# Revit family: 303_R412PX_
name_source: partatom
category: Pipe Accessories
revit_build: Autodesk Revit 2018 (Build: 20170223_1515(x64)
units: mm (PartAtom-declared; Revit-internal decimal feet)

## family parameters
Always vertical = Yes
Cut with Voids When Loaded = No
Part Type = Valve - Breaks Into
Round Connector Dimension = Use Diameter
Shared = No
Work Plane-Based = No

## types (2) — shared parameters
CAT0 = Yes
CenSd_W2_6 = 13 mm  [stored 0.0426509 ft]
D = 16 mm
D3 = 13 mm  [stored 0.0426509 ft]
Description = Straight valve with precision adjustment numberscale and protection cap, with connectoin of adapter for pipe
J12 = 5 mm  [stored 0.0164042 ft]
J12__ve = -5 mm  [stored -0.0164042 ft]
J13 = 5 mm  [stored 0.0164042 ft]
J5 = 31 mm  [stored 0.101706 ft]
L2 = 12 mm  [stored 0.0393701 ft]
L2D = 56 mm
L2D_Min = 3048 mm  [stored 10 ft]
L2__ve = -12 mm  [stored -0.0393701 ft]
L5 = 4 mm  [stored 0.0131234 ft]
L6 = 4 mm  [stored 0.0131234 ft]
L61 = 2 mm  [stored 0.00656168 ft]
L61__ve = -2 mm  [stored -0.00656168 ft]
L6__ve = -4 mm  [stored -0.0131234 ft]
LC = 51 mm  [stored 0.167323 ft]
LC1 = 28 mm  [stored 0.0918635 ft]
LC2 = 37 mm
LX = 31 mm  [stored 0.101706 ft]
M1 = 12 mm  [stored 0.0393701 ft]
M22 = 9 mm  [stored 0.0295276 ft]
Manufacturer = Giacomini
QmdConnectorList = 301;D;302;D1
URL = http://www.giacomini.com
W2 = 15 mm  [stored 0.0492126 ft]
W2D = 16 mm  [stored 0.0524934 ft]
W3 = 9 mm  [stored 0.0295276 ft]
W4 = 8 mm  [stored 0.0262467 ft]
W5 = 12 mm  [stored 0.0393701 ft]
Z1 = 11 mm
Z2 = 10 mm  [stored 0.0328084 ft]
magiPartTypeId = 303
magiProductFamilyId = R412PX*
zero-valued in all types: MC_Default_elevation

## per-type parameters (varying)
| type | B3 | D1 | G3 | K2 | R1 |
| R412PX032 | 7 mm  [stored 0.0229659 ft] | 10 mm | 10 mm  [stored 0.0328084 ft] | 8 mm  [stored 0.0262467 ft] | 8 mm  [stored 0.0262467 ft] |
| R412PX033 | 9 mm  [stored 0.0295276 ft] | 15 mm | 12 mm  [stored 0.0393701 ft] | 11 mm | 11 mm |

note: column(s) folded — value = type name in every type: magiProductCode, magiProductId

note: [stored X ft] marks values corroborated as IEEE doubles in the binary element streams (Revit-internal decimal feet)

## geometry (parser evidence)
native form markers: Sweep x1
no freeform markers — native parametric forms only
